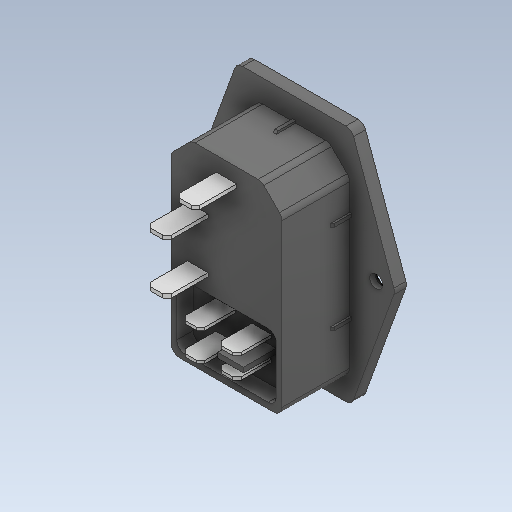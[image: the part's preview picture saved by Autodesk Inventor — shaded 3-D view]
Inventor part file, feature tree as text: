
AUTODESK INVENTOR PART (.ipt)
format: ipt  version: 2020 (Build 240168000, 168)  size: 260,608 bytes
history: native  units: in
note: dims shown in document units (in); Inventor stores cm internally (conversion verified against a paired STEP export)
features: chamfer x1
ambient origin geometry x8: Origin, YZ Plane, XZ Plane, XY Plane, X Axis, Y Axis, Z Axis, Center Point
bodies: Solid1 (feature_tree)
feature tree (1):
  chamfer  "Chamfer4"  [1 undecoded]
note: 1 required parameter value undecoded (feature->parameter linkage not recoverable at this tier; creation-order binding heuristic only, values carry confidence <= 0.55)
